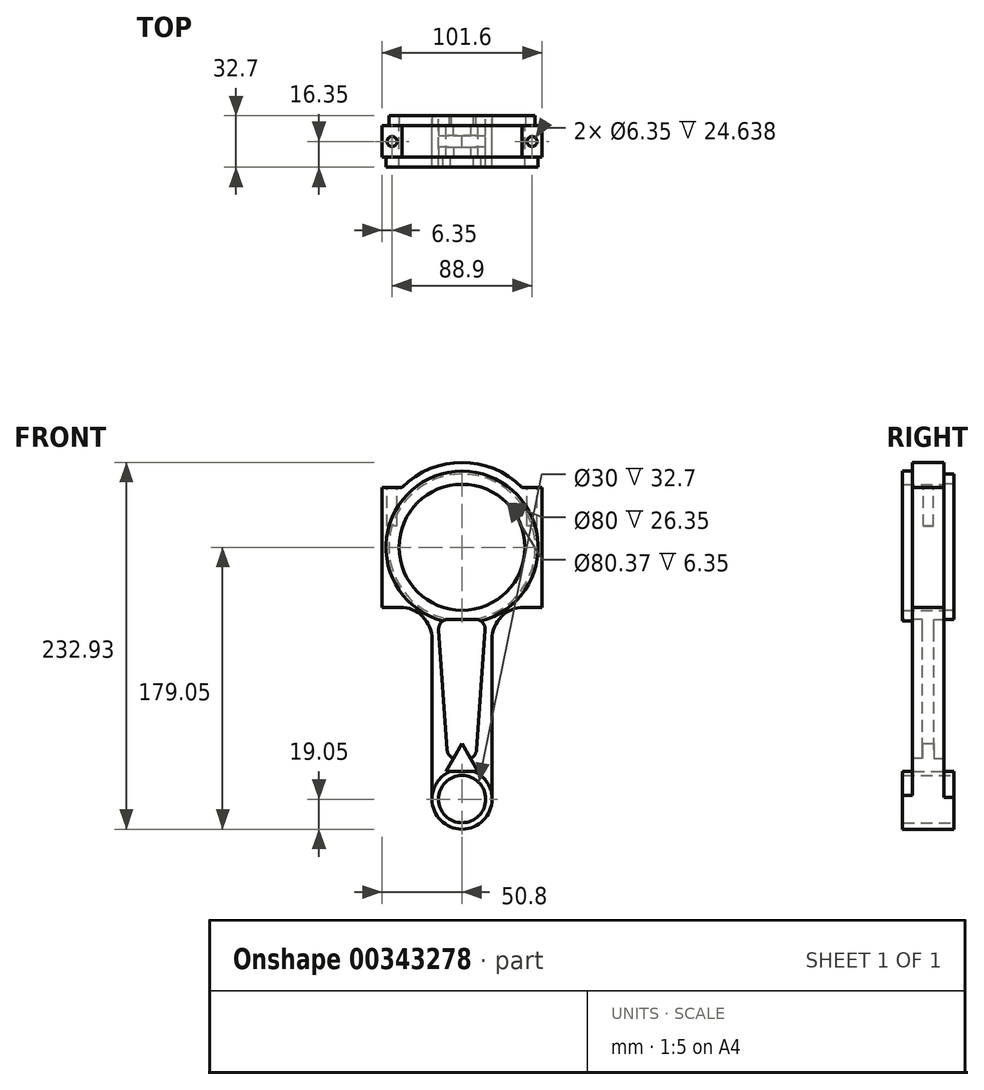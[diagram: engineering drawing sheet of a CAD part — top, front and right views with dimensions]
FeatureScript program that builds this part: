
annotation { "Feature Type Name" : "Feature", "Feature Type Description" : "" }
export const myFeature = defineFeature(function(context is Context, id is Id, definition is map)
    precondition{}
    {
        {
            var Q0;
            Q0=qCreatedBy(makeId("Front.planeOp"),FACE);
            var sketch = newSketch(context, id + "F0", { "sketchPlane" : qUnion([Q0])});
            skCircle(sketch, "E0", {"center": v(0, 0) * mm, "radius": 15 * mm});
            skCircle(sketch, "E1", {"center": v(0, 160) * mm, "radius": 40 * mm});
            skLineSegment(sketch, "E2", {"start": v(-50.8, 198.1) * mm, "end": v(-50.8, 121.9) * mm});
            skLineSegment(sketch, "E3", {"start": v(-50.8, 121.9) * mm, "end": v(-39.35, 121.9) * mm});
            skArc(sketch, "E4", {"start": v(-19.05, 101.6) * mm, "mid": v(-25, 115.95) * mm, "end": v(-39.35, 121.9) * mm});
            skLineSegment(sketch, "E5", {"start": v(-19.05, 101.6) * mm, "end": v(-19.05, 0) * mm});
            skLineSegment(sketch, "E6.MirrorCS", {"start": v(19.05, 101.6) * mm, "end": v(19.05, 0) * mm});
            skArc(sketch, "E7.MirrorCS", {"start": v(19.05, 101.6) * mm, "mid": v(25, 115.95) * mm, "end": v(39.35, 121.9) * mm});
            skLineSegment(sketch, "E8.MirrorCS", {"start": v(50.8, 198.1) * mm, "end": v(50.8, 121.9) * mm});
            skLineSegment(sketch, "E9.MirrorCS", {"start": v(50.8, 121.9) * mm, "end": v(39.35, 121.9) * mm});
            skLineSegment(sketch, "E10", {"start": v(-50.8, 198.1) * mm, "end": v(-38.1, 198.1) * mm});
            skLineSegment(sketch, "E11.MirrorCS", {"start": v(50.8, 198.1) * mm, "end": v(38.1, 198.1) * mm});
            skArc(sketch, "E12", {"start": v(38.1, 198.1) * mm, "mid": v(0, 213.88) * mm, "end": v(-38.1, 198.1) * mm});
            skArc(sketch, "E13", {"start": v(-19.05, 0) * mm, "mid": v(0, -19.05) * mm, "end": v(19.05, 0) * mm});
            skLineSegment(sketch, "E14", {"start": v(-10.27, 17.78) * mm, "end": v(10.27, 17.78) * mm});
            skLineSegment(sketch, "E15", {"start": v(-10.27, 17.78) * mm, "end": v(0, 35.56) * mm});
            skLineSegment(sketch, "E16", {"start": v(0, 35.56) * mm, "end": v(10.27, 17.78) * mm});
            skSolve(sketch);
        }
        {
            var Q0;
            Q0=makeQuery(id+"F0.imprint","IMPRINT",FACE,{"disambiguationData":[TD([[makeQuery(id+"F0.imprint","IMPRINT",EDGE,{"derivedFrom":sQuery(id+"F0.wireOp",EDGE,"E0")}),-1.0]])]});
            extrude(context, id + "F1", {"entities" : qUnion([Q0]), "endBound" : BoundingType.SYMMETRIC, "depth" : 20 * mm});
        }
        {
            var Q0;
            Q0=makeQuery(id+"F1.opExtrude","CAP_FACE",FACE,{"disambiguationData":[OSD([sQuery(id+"F0.wireOp",EDGE,"E0"),sQuery(id+"F0.wireOp",EDGE,"E1"),sQuery(id+"F0.wireOp",EDGE,"E2"),sQuery(id+"F0.wireOp",EDGE,"E3"),sQuery(id+"F0.wireOp",EDGE,"E4"),sQuery(id+"F0.wireOp",EDGE,"E5"),sQuery(id+"F0.wireOp",EDGE,"E6.MirrorCS"),sQuery(id+"F0.wireOp",EDGE,"E7.MirrorCS"),sQuery(id+"F0.wireOp",EDGE,"E8.MirrorCS"),sQuery(id+"F0.wireOp",EDGE,"E9.MirrorCS"),sQuery(id+"F0.wireOp",EDGE,"E10"),sQuery(id+"F0.wireOp",EDGE,"E11.MirrorCS"),sQuery(id+"F0.wireOp",EDGE,"E12"),sQuery(id+"F0.wireOp",EDGE,"E13")])],"isStart":true});
            var sketch = newSketch(context, id + "F2", { "sketchPlane" : qUnion([Q0])});
            skLineSegment(sketch, "E17", {"start": v(-8.42, 114.3) * mm, "end": v(8.42, 114.3) * mm});
            skLineSegment(sketch, "E18", {"start": v(14.75, 107.5) * mm, "end": v(9.31, 31.3) * mm});
            skLineSegment(sketch, "E19", {"start": v(2.98, 25.4) * mm, "end": v(-2.98, 25.4) * mm});
            skLineSegment(sketch, "E20", {"start": v(-9.31, 31.3) * mm, "end": v(-14.75, 107.5) * mm});
            skPoint(sketch, "E21.visualSharp", {"position": v(-15.24, 114.3) * mm});
            skArc(sketch, "E21.filletArc", {"start": v(-8.42, 114.3) * mm, "mid": v(-13.07, 112.28) * mm, "end": v(-14.75, 107.5) * mm});
            skPoint(sketch, "E22.visualSharp", {"position": v(15.24, 114.3) * mm});
            skArc(sketch, "E22.filletArc", {"start": v(14.75, 107.5) * mm, "mid": v(13.07, 112.28) * mm, "end": v(8.42, 114.3) * mm});
            skPoint(sketch, "E23.visualSharp", {"position": v(-8.9, 25.4) * mm});
            skArc(sketch, "E23.filletArc", {"start": v(-9.31, 31.3) * mm, "mid": v(-7.3, 27.1) * mm, "end": v(-2.98, 25.4) * mm});
            skPoint(sketch, "E24.visualSharp", {"position": v(8.89, 25.4) * mm});
            skArc(sketch, "E24.filletArc", {"start": v(2.98, 25.4) * mm, "mid": v(7.3, 27.1) * mm, "end": v(9.31, 31.3) * mm});
            skSolve(sketch);
        }
        {
            var Q0;
            Q0=makeQuery(id+"F2.imprint","IMPRINT",FACE,{"disambiguationData":[TD([[makeQuery(id+"F2.imprint","IMPRINT",EDGE,{"derivedFrom":sQuery(id+"F2.wireOp",EDGE,"E17")}),-1.0]])]});
            extrude(context, id + "F3", {"entities" : qUnion([Q0]), "operationType" : NewBodyOperationType.REMOVE, "oppositeDirection" : true, "depth" : 6.35 * mm});
        }
        {
            var Q0;
            Q0=makeQuery(id+"F1.opExtrude","CAP_FACE",FACE,{"disambiguationData":[OSD([sQuery(id+"F0.wireOp",EDGE,"E0"),sQuery(id+"F0.wireOp",EDGE,"E1"),sQuery(id+"F0.wireOp",EDGE,"E2"),sQuery(id+"F0.wireOp",EDGE,"E3"),sQuery(id+"F0.wireOp",EDGE,"E4"),sQuery(id+"F0.wireOp",EDGE,"E5"),sQuery(id+"F0.wireOp",EDGE,"E6.MirrorCS"),sQuery(id+"F0.wireOp",EDGE,"E7.MirrorCS"),sQuery(id+"F0.wireOp",EDGE,"E8.MirrorCS"),sQuery(id+"F0.wireOp",EDGE,"E9.MirrorCS"),sQuery(id+"F0.wireOp",EDGE,"E10"),sQuery(id+"F0.wireOp",EDGE,"E11.MirrorCS"),sQuery(id+"F0.wireOp",EDGE,"E12"),sQuery(id+"F0.wireOp",EDGE,"E13")])],"isStart":false});
            var sketch = newSketch(context, id + "F4", { "sketchPlane" : qUnion([Q0])});
            skLineSegment(sketch, "E25", {"start": v(-8.55, 114.3) * mm, "end": v(8.29, 114.3) * mm});
            skLineSegment(sketch, "E26", {"start": v(14.62, 107.5) * mm, "end": v(9.18, 31.3) * mm});
            skLineSegment(sketch, "E27", {"start": v(2.84, 25.4) * mm, "end": v(-3.1, 25.4) * mm});
            skLineSegment(sketch, "E28", {"start": v(-9.44, 31.3) * mm, "end": v(-14.89, 107.5) * mm});
            skPoint(sketch, "E29.visualSharp", {"position": v(-15.37, 114.3) * mm});
            skArc(sketch, "E29.filletArc", {"start": v(-8.55, 114.3) * mm, "mid": v(-13.2, 112.28) * mm, "end": v(-14.89, 107.5) * mm});
            skPoint(sketch, "E30.visualSharp", {"position": v(15.1, 114.3) * mm});
            skArc(sketch, "E30.filletArc", {"start": v(14.62, 107.5) * mm, "mid": v(12.93, 112.28) * mm, "end": v(8.29, 114.3) * mm});
            skPoint(sketch, "E31.visualSharp", {"position": v(-9.02, 25.4) * mm});
            skArc(sketch, "E31.filletArc", {"start": v(-9.44, 31.3) * mm, "mid": v(-7.44, 27.1) * mm, "end": v(-3.1, 25.4) * mm});
            skPoint(sketch, "E32.visualSharp", {"position": v(8.76, 25.4) * mm});
            skArc(sketch, "E32.filletArc", {"start": v(2.84, 25.4) * mm, "mid": v(7.17, 27.1) * mm, "end": v(9.18, 31.3) * mm});
            skSolve(sketch);
        }
        {
            var Q0;
            Q0=makeQuery(id+"F4.imprint","IMPRINT",FACE,{"disambiguationData":[TD([[makeQuery(id+"F4.imprint","IMPRINT",EDGE,{"derivedFrom":sQuery(id+"F4.wireOp",EDGE,"E25")}),-1.0]])]});
            extrude(context, id + "F5", {"entities" : qUnion([Q0]), "operationType" : NewBodyOperationType.REMOVE, "oppositeDirection" : true, "depth" : 6.35 * mm});
        }
        {
            var Q0;
            Q0=makeQuery(id+"F1.opExtrude","CAP_FACE",FACE,{"disambiguationData":[OSD([sQuery(id+"F0.wireOp",EDGE,"E0"),sQuery(id+"F0.wireOp",EDGE,"E1"),sQuery(id+"F0.wireOp",EDGE,"E2"),sQuery(id+"F0.wireOp",EDGE,"E3"),sQuery(id+"F0.wireOp",EDGE,"E4"),sQuery(id+"F0.wireOp",EDGE,"E5"),sQuery(id+"F0.wireOp",EDGE,"E6.MirrorCS"),sQuery(id+"F0.wireOp",EDGE,"E7.MirrorCS"),sQuery(id+"F0.wireOp",EDGE,"E8.MirrorCS"),sQuery(id+"F0.wireOp",EDGE,"E9.MirrorCS"),sQuery(id+"F0.wireOp",EDGE,"E10"),sQuery(id+"F0.wireOp",EDGE,"E11.MirrorCS"),sQuery(id+"F0.wireOp",EDGE,"E12"),sQuery(id+"F0.wireOp",EDGE,"E13")])],"isStart":false});
            var sketch = newSketch(context, id + "F6", { "sketchPlane" : qUnion([Q0])});
            skCircle(sketch, "E33", {"center": v(0, 0) * mm, "radius": 14.78 * mm});
            skCircle(sketch, "E34", {"center": v(0, 0) * mm, "radius": 19.18 * mm});
            skCircle(sketch, "E35", {"center": v(0, 160) * mm, "radius": 39.98 * mm});
            skCircle(sketch, "E36", {"center": v(0, 160) * mm, "radius": 48.3 * mm});
            skSolve(sketch);
        }
        {
            var Q0;
            Q0=makeQuery(id+"F6.imprint","IMPRINT",FACE,{"disambiguationData":[TD([[makeQuery(id+"F6.imprint","IMPRINT",EDGE,{"derivedFrom":makeQuery(id+"F1.opExtrude","CAP_EDGE",EDGE,{"disambiguationData":[OSD([sQuery(id+"F0.wireOp",EDGE,"E1")])],"isStart":false})}),-1.0]])]});
            var Q1;
            Q1=makeQuery(id+"F6.imprint","IMPRINT",FACE,{"disambiguationData":[TD([[makeQuery(id+"F6.imprint","IMPRINT",EDGE,{"derivedFrom":makeQuery(id+"F1.opExtrude","CAP_EDGE",EDGE,{"disambiguationData":[OSD([sQuery(id+"F0.wireOp",EDGE,"E0")])],"isStart":false})}),-1.0]])]});
            extrude(context, id + "F7", {"entities" : qUnion([Q0, Q1]), "operationType" : NewBodyOperationType.ADD, "endBound" : BoundingType.SYMMETRIC, "depth" : 12.7 * mm});
        }
        {
            var Q0;
            Q0=makeQuery(id+"F1.opExtrude","CAP_FACE",FACE,{"disambiguationData":[OSD([sQuery(id+"F0.wireOp",EDGE,"E0"),sQuery(id+"F0.wireOp",EDGE,"E1"),sQuery(id+"F0.wireOp",EDGE,"E2"),sQuery(id+"F0.wireOp",EDGE,"E3"),sQuery(id+"F0.wireOp",EDGE,"E4"),sQuery(id+"F0.wireOp",EDGE,"E5"),sQuery(id+"F0.wireOp",EDGE,"E6.MirrorCS"),sQuery(id+"F0.wireOp",EDGE,"E7.MirrorCS"),sQuery(id+"F0.wireOp",EDGE,"E8.MirrorCS"),sQuery(id+"F0.wireOp",EDGE,"E9.MirrorCS"),sQuery(id+"F0.wireOp",EDGE,"E10"),sQuery(id+"F0.wireOp",EDGE,"E11.MirrorCS"),sQuery(id+"F0.wireOp",EDGE,"E12"),sQuery(id+"F0.wireOp",EDGE,"E13")])],"isStart":true});
            var sketch = newSketch(context, id + "F8", { "sketchPlane" : qUnion([Q0])});
            skCircle(sketch, "E37", {"center": v(0, 0) * mm, "radius": 14.94 * mm});
            skCircle(sketch, "E38", {"center": v(0, 0) * mm, "radius": 19.1 * mm});
            skCircle(sketch, "E39", {"center": v(0, 160) * mm, "radius": 40.19 * mm});
            skCircle(sketch, "E40", {"center": v(0, 160) * mm, "radius": 46.47 * mm});
            skSolve(sketch);
        }
        {
            var Q0;
            Q0=makeQuery(id+"F8.imprint","IMPRINT",FACE,{"disambiguationData":[TD([[makeQuery(id+"F8.imprint","IMPRINT",EDGE,{"derivedFrom":sQuery(id+"F8.wireOp",EDGE,"E39")}),-1.0]])]});
            var Q1;
            Q1=makeQuery(id+"F8.imprint","IMPRINT",FACE,{"disambiguationData":[TD([[makeQuery(id+"F8.imprint","IMPRINT",EDGE,{"derivedFrom":makeQuery(id+"F1.opExtrude","CAP_EDGE",EDGE,{"disambiguationData":[OSD([sQuery(id+"F0.wireOp",EDGE,"E0")])],"isStart":true})}),1.0]])]});
            extrude(context, id + "F9", {"entities" : qUnion([Q0, Q1]), "operationType" : NewBodyOperationType.ADD, "endBound" : BoundingType.SYMMETRIC, "depth" : 12.7 * mm});
        }
        {
            var Q0;
            Q0=makeQuery(id+"F1.opExtrude","SWEPT_FACE",FACE,{"disambiguationData":[OSD([sQuery(id+"F0.wireOp",EDGE,"E11.MirrorCS")])]});
            var sketch = newSketch(context, id + "F10", { "sketchPlane" : qUnion([Q0])});
            skCircle(sketch, "E41", {"center": v(44.45, 0) * mm, "radius": 3.18 * mm});
            skCircle(sketch, "E42", {"center": v(-44.45, 0) * mm, "radius": 3.18 * mm});
            skSolve(sketch);
        }
        {
            var Q0;
            Q0=makeQuery(id+"F10.imprint","IMPRINT",FACE,{"disambiguationData":[TD([[makeQuery(id+"F10.imprint","IMPRINT",EDGE,{"derivedFrom":sQuery(id+"F10.wireOp",EDGE,"E42")}),1.0]])]});
            var Q1;
            Q1=makeQuery(id+"F10.imprint","IMPRINT",FACE,{"disambiguationData":[TD([[makeQuery(id+"F10.imprint","IMPRINT",EDGE,{"derivedFrom":sQuery(id+"F10.wireOp",EDGE,"E41")}),1.0]])]});
            extrude(context, id + "F11", {"entities" : qUnion([Q0, Q1]), "operationType" : NewBodyOperationType.REMOVE, "oppositeDirection" : true, "depth" : 24.64 * mm});
        }
    });
